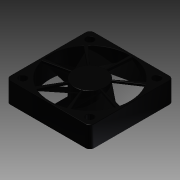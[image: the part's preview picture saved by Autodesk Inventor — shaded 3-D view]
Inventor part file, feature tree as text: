
AUTODESK INVENTOR PART (.ipt)
format: ipt  version: 2015 (Build 190159000, 159)  size: 437,248 bytes
history: native  units: in
note: dims shown in document units (in); Inventor stores cm internally (conversion verified against a paired STEP export)
features: sketch x6, extrude x4, plane x1, pattern_circular x1, fillet x1, projected_geometry x1
ambient origin geometry x8: Origin, YZ Plane, XZ Plane, XY Plane, X Axis, Y Axis, Z Axis, Center Point
bodies: Solid1 (feature_tree)
feature tree (14):
  extrude  "Extrusion1"  Depth=1.5748in
  extrude  "Extrusion2"  Depth=0.3937in
  extrude  "Extrusion3"  Depth=1.2598in
  sketch  "Sketch4"  dims[d7=1.2598in d8=0.1378in]
  plane  "Work Plane1"
  extrude  "Extrusion4"  Depth=0.1378in
  sketch  "Sketch6"  dims[d10=0.0787in d11=1.4961in d12=0.3937in d13=0.0in d14=0.0787in d15=0.0787in d16=0.5906in d22=0.0394in d23=0.0in d25=0.0344in d30=2.7559in d32=360.0deg d37=60.0deg d38=0.0157in d41=0.0079in d43=0.7402in d44=0.0in d45=0.0079in d46=0.2716in d48=2.7559in d49=360.0deg d51=0.0079in]
  pattern_circular  "Circular Pattern1"  [2 undecoded]
  fillet  "Fillet1"  Radius=0.3937in
  sketch  "Sketch1"  dims[d0=1.5748in d1=1.5748in]
  sketch  "Sketch2"  dims[d2=0.3937in d3=0.0in d4=1.5748in]
  sketch  "Sketch3"  dims[d5=1.5748in d6=1.2598in]
  sketch  "Sketch5"  dims[d9=0.0787in]
  projected_geometry  "Projected Loop1"
note: 2 required parameter values undecoded (feature->parameter linkage not recoverable at this tier; creation-order binding heuristic only, values carry confidence <= 0.55)
